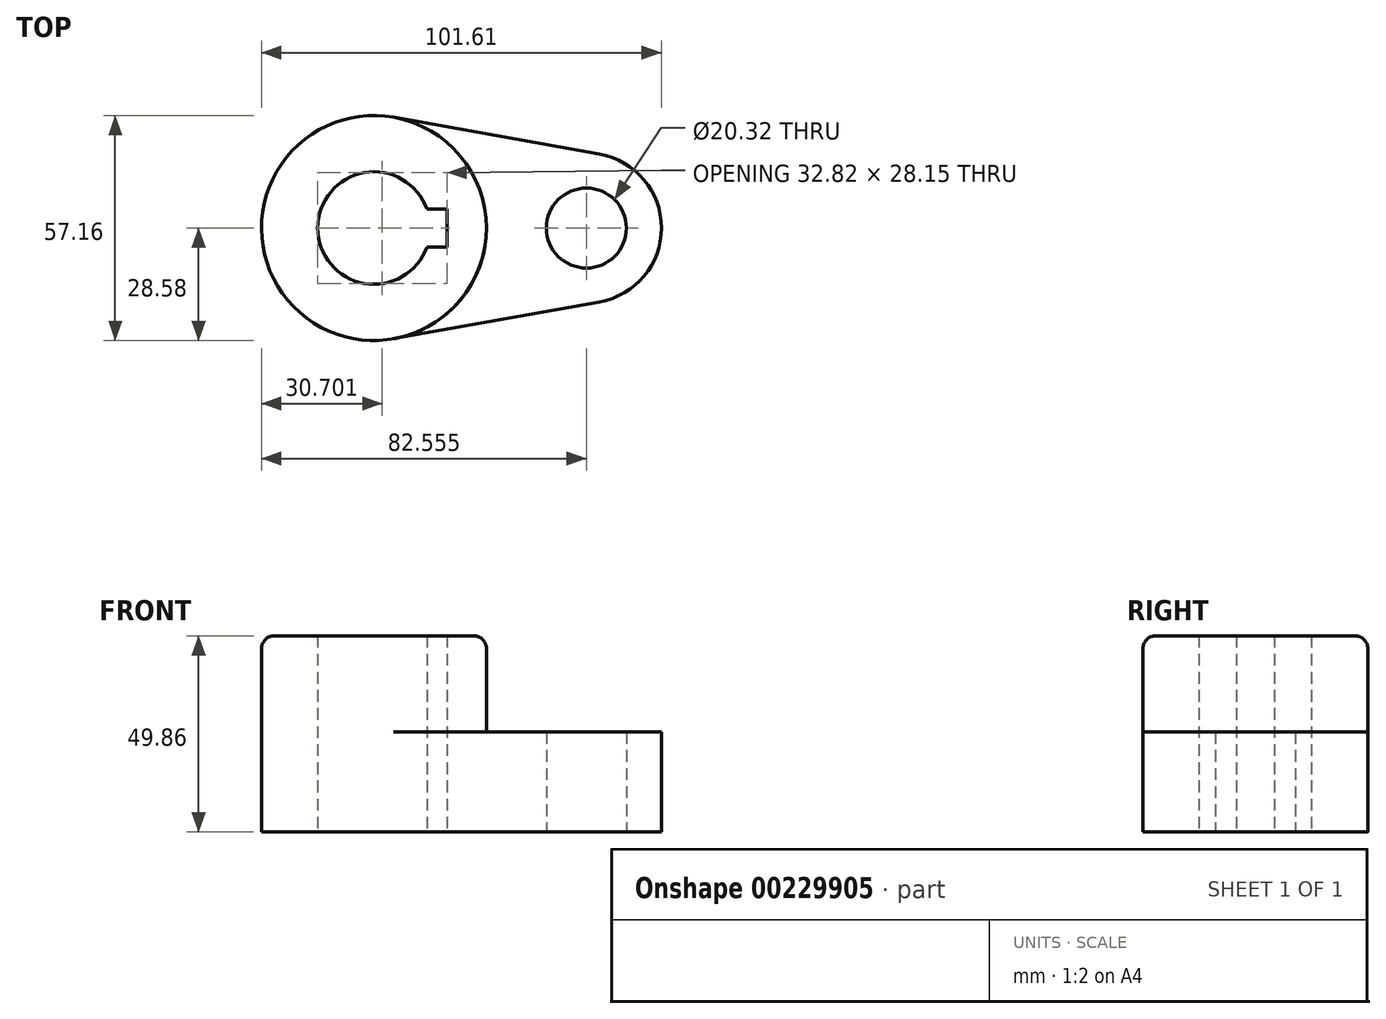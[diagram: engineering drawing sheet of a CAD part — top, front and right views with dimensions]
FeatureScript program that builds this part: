
annotation { "Feature Type Name" : "Feature", "Feature Type Description" : "" }
export const myFeature = defineFeature(function(context is Context, id is Id, definition is map)
    precondition{}
    {
        {
            var Q0;
            Q0=qCreatedBy(makeId("Top.planeOp"),FACE);
            var sketch = newSketch(context, id + "F0", { "sketchPlane" : qUnion([Q0])});
            skCircle(sketch, "E0", {"center": v(0, 0) * mm, "radius": 28.58 * mm});
            skArc(sketch, "E1", {"start": v(13.45, 4.83) * mm, "mid": v(-14.29, 0) * mm, "end": v(13.45, -4.83) * mm});
            skCircle(sketch, "E2", {"center": v(53.98, 0) * mm, "radius": 10.16 * mm});
            skArc(sketch, "E3", {"start": v(57.34, -18.75) * mm, "mid": v(73.03, 0) * mm, "end": v(57.34, 18.75) * mm});
            skLineSegment(sketch, "E4", {"start": v(57.34, 18.75) * mm, "end": v(5.04, 28.13) * mm});
            skLineSegment(sketch, "E5", {"start": v(57.34, -18.75) * mm, "end": v(0, -29.03) * mm});
            skLineSegment(sketch, "E6", {"start": v(18.53, 0) * mm, "end": v(18.53, 4.83) * mm});
            skLineSegment(sketch, "E7", {"start": v(18.53, 0) * mm, "end": v(18.53, -4.83) * mm});
            skLineSegment(sketch, "E8", {"start": v(18.53, 4.83) * mm, "end": v(13.45, 4.83) * mm});
            skLineSegment(sketch, "E9", {"start": v(18.53, -4.83) * mm, "end": v(13.45, -4.83) * mm});
            skPoint(sketch, "E10.start.orphan", {"position": v(-14.29, 0) * mm});
            skSolve(sketch);
        }
        {
            var Q0;
            Q0=makeQuery(id+"F0.imprint","IMPRINT",FACE,{"disambiguationData":[TD([[makeQuery(id+"F0.imprint","IMPRINT",EDGE,{"derivedFrom":sQuery(id+"F0.wireOp",EDGE,"E2")}),-1.0]])]});
            var Q1;
            Q1=makeQuery(id+"F0.imprint","IMPRINT",FACE,{"disambiguationData":[TD([[makeQuery(id+"F0.imprint","IMPRINT",EDGE,{"derivedFrom":sQuery(id+"F0.wireOp",EDGE,"E1")}),-1.0]])]});
            extrude(context, id + "F1", {"entities" : qUnion([Q0, Q1]), "depth" : 25.4 * mm});
        }
        {
            var Q0;
            Q0=makeQuery(id+"F1.opExtrude","CAP_FACE",FACE,{"disambiguationData":[OSD([sQuery(id+"F0.wireOp",EDGE,"E0"),sQuery(id+"F0.wireOp",EDGE,"E1"),sQuery(id+"F0.wireOp",EDGE,"E2"),sQuery(id+"F0.wireOp",EDGE,"E3"),sQuery(id+"F0.wireOp",EDGE,"E4"),sQuery(id+"F0.wireOp",EDGE,"E5"),sQuery(id+"F0.wireOp",EDGE,"E6"),sQuery(id+"F0.wireOp",EDGE,"E7"),sQuery(id+"F0.wireOp",EDGE,"E8"),sQuery(id+"F0.wireOp",EDGE,"E9")])],"isStart":false});
            var sketch = newSketch(context, id + "F2", { "sketchPlane" : qUnion([Q0])});
            skArc(sketch, "E11.0", {"start": v(13.45, 4.83) * mm, "mid": v(-14.29, 0) * mm, "end": v(13.45, -4.83) * mm});
            skLineSegment(sketch, "E12.0", {"start": v(18.53, -4.83) * mm, "end": v(18.53, 4.83) * mm});
            skLineSegment(sketch, "E13.0", {"start": v(18.53, 4.83) * mm, "end": v(13.45, 4.83) * mm});
            skLineSegment(sketch, "E14.0", {"start": v(18.53, -4.83) * mm, "end": v(13.45, -4.83) * mm});
            skCircle(sketch, "E15", {"center": v(0, 0) * mm, "radius": 28.58 * mm});
            skSolve(sketch);
        }
        {
            var Q0;
            Q0=makeQuery(id+"F2.imprint","IMPRINT",FACE,{"disambiguationData":[TD([[makeQuery(id+"F2.imprint","IMPRINT",EDGE,{"derivedFrom":sQuery(id+"F2.wireOp",EDGE,"E11.0")}),-1.0]])]});
            extrude(context, id + "F3", {"entities" : qUnion([Q0]), "operationType" : NewBodyOperationType.ADD, "depth" : 24.46 * mm});
        }
        {
            var Q0;
            Q0=makeQuery(id+"F3.opExtrude","CAP_EDGE",EDGE,{"disambiguationData":[OSD([sQuery(id+"F2.wireOp",EDGE,"E15")])],"isStart":false});
            fillet(context, id + "F4", {"entities" : qUnion([Q0]), "radius" : 3.3 * mm, "tangentPropagation" : true, "allowEdgeOverflow" : false});
        }
    });
